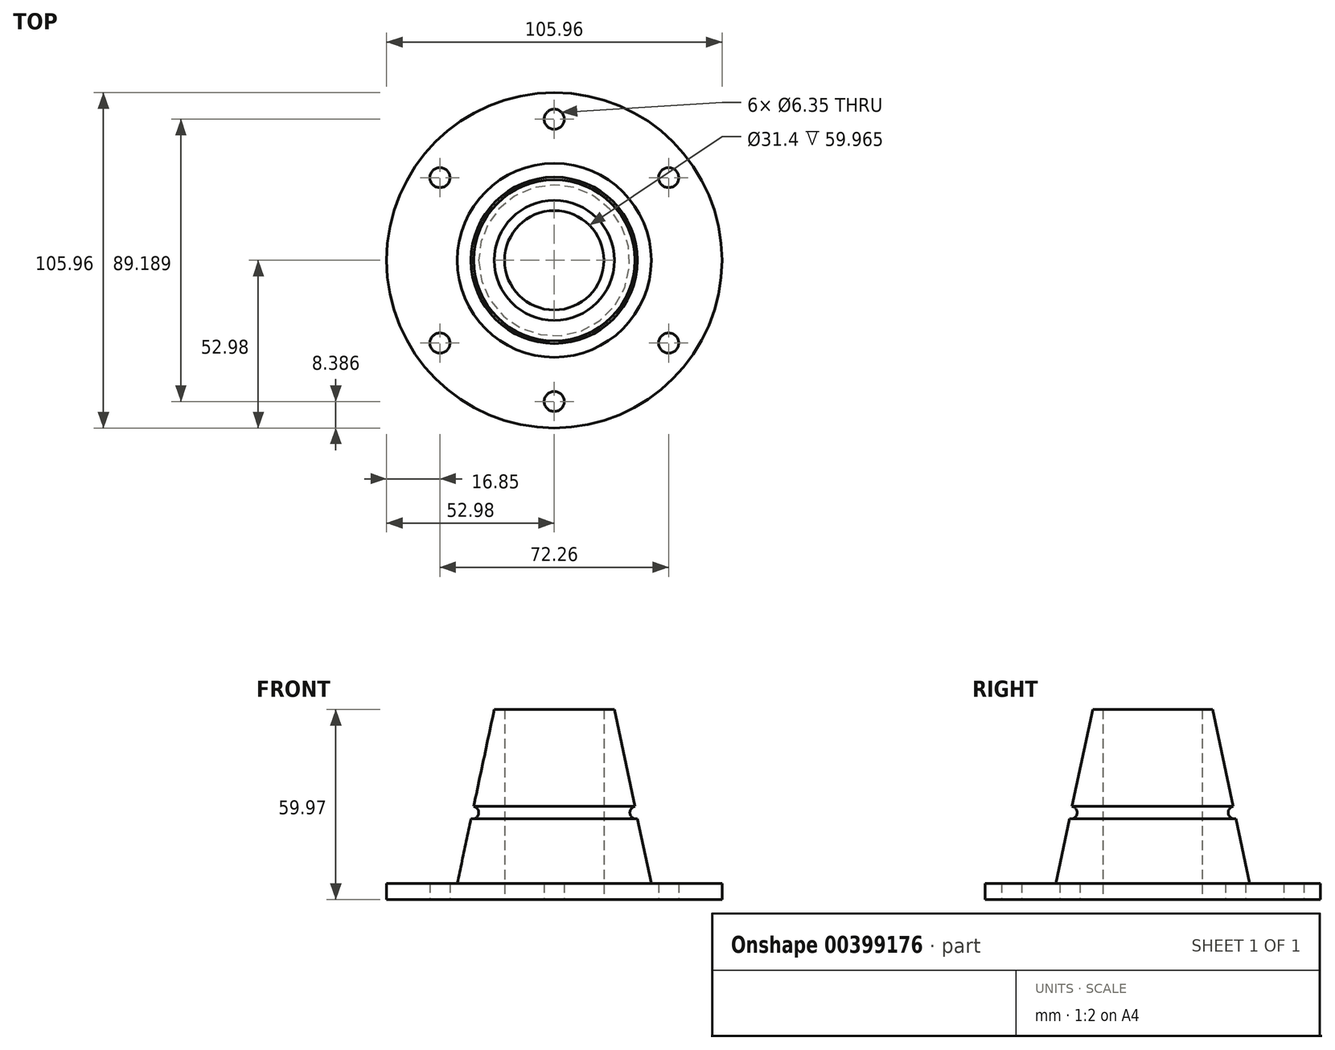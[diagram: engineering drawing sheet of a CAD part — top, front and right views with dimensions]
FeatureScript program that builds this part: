
annotation { "Feature Type Name" : "Feature", "Feature Type Description" : "" }
export const myFeature = defineFeature(function(context is Context, id is Id, definition is map)
    precondition{}
    {
        {
            var Q0;
            Q0=qCreatedBy(makeId("Front.planeOp"),FACE);
            var sketch = newSketch(context, id + "F0", { "sketchPlane" : qUnion([Q0])});
            skLineSegment(sketch, "E0", {"start": v(0, 0) * mm, "end": v(0, 60.5) * mm});
            skLineSegment(sketch, "E1.left", {"start": v(15.7, 5.08) * mm, "end": v(15.7, 59.97) * mm});
            skLineSegment(sketch, "E2.top", {"start": v(52.98, 5.08) * mm, "end": v(15.7, 5.08) * mm});
            skLineSegment(sketch, "E2.left", {"start": v(52.98, 0) * mm, "end": v(52.98, 5.08) * mm});
            skLineSegment(sketch, "E2.right", {"start": v(0, 0) * mm, "end": v(0, 5.08) * mm});
            skPoint(sketch, "E3.orphan", {"position": v(33.02, 60.5) * mm});
            skPoint(sketch, "E4.trimOffspring.start.orphan", {"position": v(15.7, 0) * mm});
            skLineSegment(sketch, "E5", {"start": v(15.7, 0) * mm, "end": v(52.98, 0) * mm});
            skLineSegment(sketch, "E6", {"start": v(15.7, 59.97) * mm, "end": v(18.97, 59.97) * mm});
            skLineSegment(sketch, "E7", {"start": v(18.97, 59.97) * mm, "end": v(25.46, 29.4) * mm});
            skArc(sketch, "E8", {"start": v(25.46, 29.4) * mm, "mid": v(23.9, 27.01) * mm, "end": v(26.3, 25.46) * mm});
            skLineSegment(sketch, "E9.trimOffspring", {"start": v(26.3, 25.46) * mm, "end": v(30.63, 5.08) * mm});
            skLineSegment(sketch, "E10", {"start": v(15.7, 5.08) * mm, "end": v(15.7, 0) * mm});
            skSolve(sketch);
        }
        {
            var Q0;
            Q0 = qSketchRegion(id + "F0", true);
            var Q1;
            Q1=sQuery(id+"F0.wireOp",EDGE,"E0");
            revolve(context, id + "F1", {"entities" : qUnion([Q0]), "axis" : qUnion([Q1]), "revolveType" : RevolveType.FULL});
        }
        {
            var Q0;
            Q0=makeQuery(id+"F1.opRevolve","SWEPT_FACE",FACE,{"disambiguationData":[OSD([sQuery(id+"F0.wireOp",EDGE,"E5")])]});
            var sketch = newSketch(context, id + "F2", { "sketchPlane" : qUnion([Q0])});
            skCircle(sketch, "E11", {"center": v(0, 0) * mm, "radius": 44.6 * mm});
            skPoint(sketch, "E12", {"position": v(0, 44.6) * mm});
            skPoint(sketch, "E13", {"position": v(0, -44.6) * mm});
            skPoint(sketch, "E14", {"position": v(36.13, 26.14) * mm});
            skPoint(sketch, "E15", {"position": v(36.13, -26.14) * mm});
            skPoint(sketch, "E16", {"position": v(-36.13, -26.14) * mm});
            skPoint(sketch, "E17", {"position": v(-36.13, 26.14) * mm});
            skSolve(sketch);
        }
        {
            var Q0;
            Q0=sQuery(id+"F2.wireOp",VERTEX,"E17");
            var Q1;
            Q1=sQuery(id+"F2.wireOp",VERTEX,"E12");
            var Q2;
            Q2=sQuery(id+"F2.wireOp",VERTEX,"E14");
            var Q3;
            Q3=sQuery(id+"F2.wireOp",VERTEX,"E15");
            var Q4;
            Q4=sQuery(id+"F2.wireOp",VERTEX,"E13");
            var Q5;
            Q5=sQuery(id+"F2.wireOp",VERTEX,"E16");
            var Q6;
            Q6=makeQuery(id+"F1.opRevolve","SWEPT_BODY",BODY,{"disambiguationData":[OSD([sQuery(id+"F0.wireOp",EDGE,"E1.left"),sQuery(id+"F0.wireOp",EDGE,"E2.top"),sQuery(id+"F0.wireOp",EDGE,"E2.left"),sQuery(id+"F0.wireOp",EDGE,"E5"),sQuery(id+"F0.wireOp",EDGE,"E6"),sQuery(id+"F0.wireOp",EDGE,"E7"),sQuery(id+"F0.wireOp",EDGE,"E8"),sQuery(id+"F0.wireOp",EDGE,"E9.trimOffspring"),sQuery(id+"F0.wireOp",EDGE,"E10")])]});
            hole(context, id + "F3", {"style" : HoleStyle.SIMPLE, "endStyle" : HoleEndStyle.THROUGH, "holeDiameter" : 6.35 * mm, "isTappedThrough" : true, "tappedDepth" : 12.7 * mm, "tapClearance" : 3, "locations" : qUnion([Q0, Q1, Q2, Q3, Q4, Q5]), "scope" : qUnion([Q6])});
        }
    });
